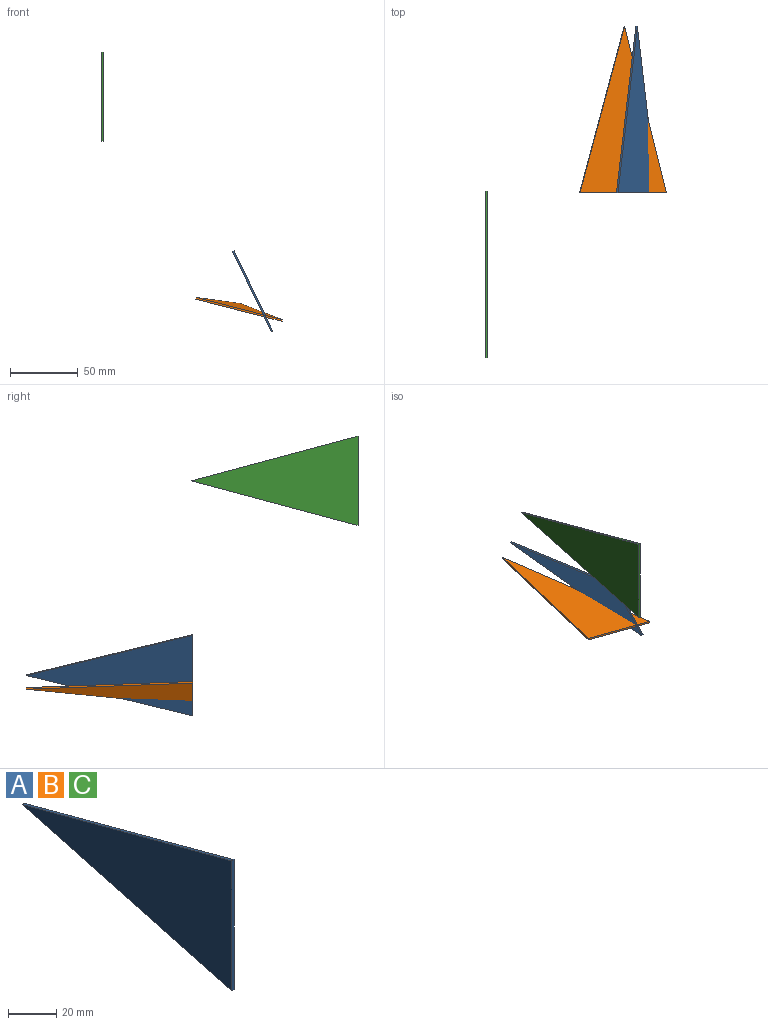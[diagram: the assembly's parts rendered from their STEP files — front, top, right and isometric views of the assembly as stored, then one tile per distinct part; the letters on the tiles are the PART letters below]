
ASSEMBLY  parts=3 mates=1
PART A: 5 faces, bbox 1.3x122.7x65.7 mm
  f0: plane 122.67x32.87mm, normal (0,0.26,0.97), area 161.3mm2, adj f1,f2,f3,f4
  f1: plane 65.74x1.27mm, normal (0,-1,0), area 83.5mm2, adj f0,f2,f3,f4
  f2: plane 122.67x32.87mm, normal (0,0.26,-0.97), area 161.3mm2, adj f0,f1,f3,f4
  f3: plane 122.67x65.74mm, normal (1,0,0), area 4032.3mm2, adj f0,f1,f2
  f4: plane 122.67x65.74mm, normal (-1,0,0), area 4032.3mm2, adj f0,f1,f2
PART B: same geometry as A
PART C: same geometry as A
PLACE A rot(axis=(0,1,0),154.3deg) t=(88.91,105.21,-600.95)mm
PLACE B rot(axis=(0.02,1,0.01),104.5deg) t=(240.66,105.02,-407.33)mm
PLACE C t=(-151.81,-16.64,106.51)mm
MATE ball B.f4 <-> A.f3  axis (0.25,-0.03,0.97) through (-33.98,-276.18,-348.72)mm
